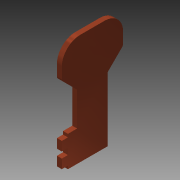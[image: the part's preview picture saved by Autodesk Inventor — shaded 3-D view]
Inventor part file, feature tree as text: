
AUTODESK INVENTOR PART (.ipt)
format: ipt  version: 2014 SP1 (Build 180222100, 222)  size: 128,000 bytes
history: native  units: mm
features: sheet_metal_op x3, chamfer x2, sketch x2, other x2
ambient origin geometry x8: Origin, YZ Plane, XZ Plane, XY Plane, X Axis, Y Axis, Z Axis, Center Point
bodies: Solid1 (feature_tree)
feature tree (9):
  sheet_metal_op  "Face1"
  chamfer  "Corner Round1"
  chamfer  "Corner Round2"
  sheet_metal_op  "Face2"
  sketch  "Sketch1"  dims[d0=10.0mm]
  other  "Plate1"
  sketch  "Sketch2"  dims[d1=45.0deg d2=45.0deg d3=5.0mm d4=5.0mm d5=10.0mm d6=1.6mm d7=1.0mm d8=10.0mm d9=6.0mm d10=2.0mm d11=3.0mm d12=3.0mm d13=1.0mm d14=1.0mm d15=2.0mm d16=2.0mm d17=3.0mm d18=6.0mm d19=1.6mm d20=1.6mm d21=0.8mm d22=3.2mm d23=1.6mm]
  other  "Plate2"
  sheet_metal_op  "Bend1"
